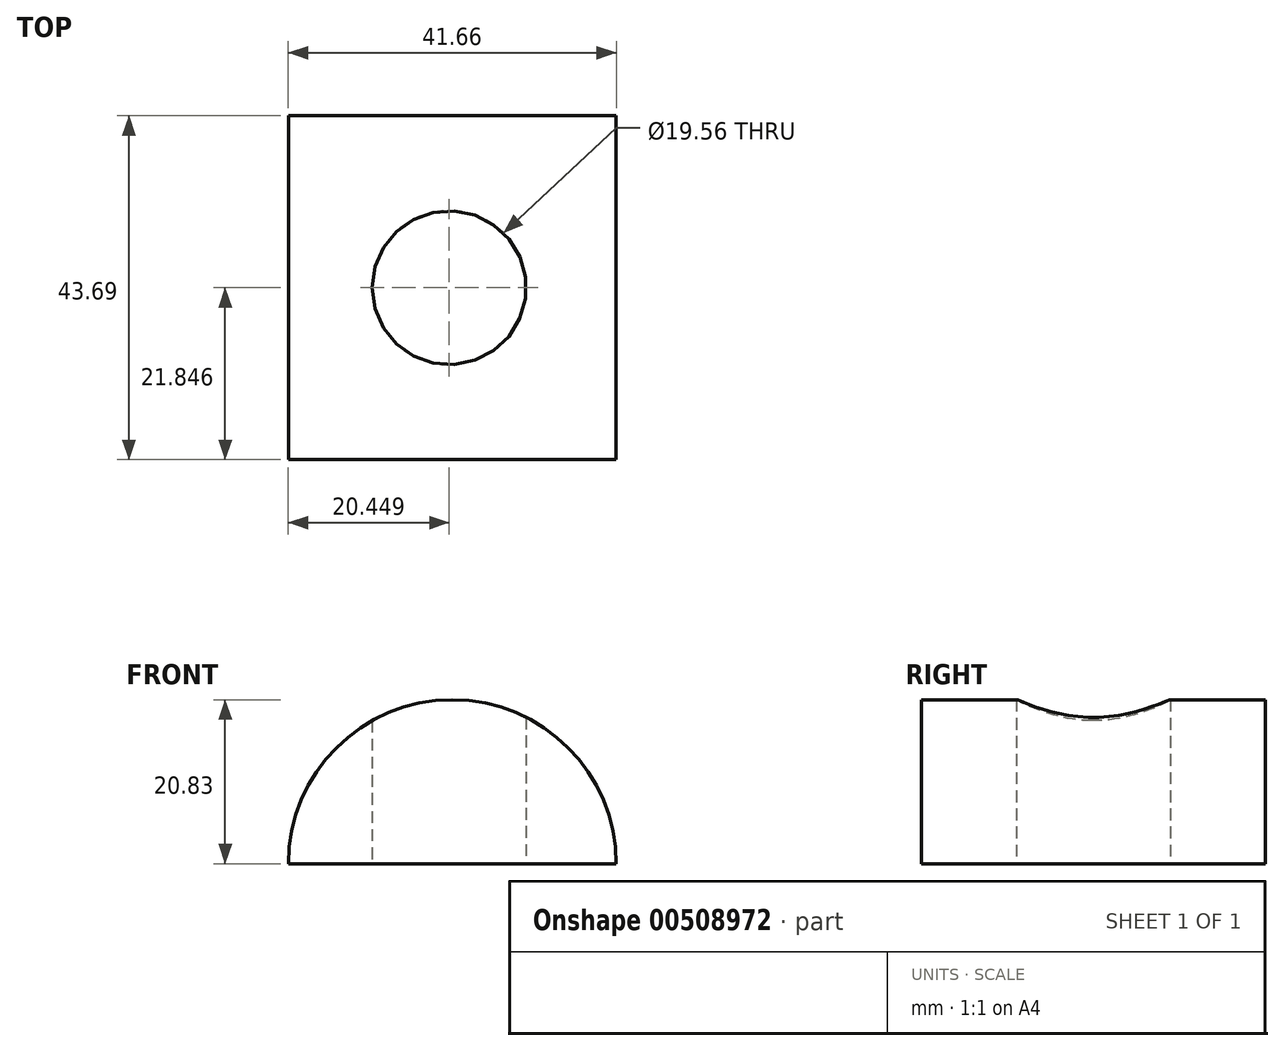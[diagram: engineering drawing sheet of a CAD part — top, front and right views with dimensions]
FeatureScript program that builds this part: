
annotation { "Feature Type Name" : "Feature", "Feature Type Description" : "" }
export const myFeature = defineFeature(function(context is Context, id is Id, definition is map)
    precondition{}
    {
        {
            var Q0;
            Q0=qCreatedBy(makeId("Top.planeOp"),FACE);
            var sketch = newSketch(context, id + "F0", { "sketchPlane" : qUnion([Q0])});
            skLineSegment(sketch, "E0.bottom", {"start": v(0, 0) * mm, "end": v(43.18, 0) * mm});
            skLineSegment(sketch, "E0.top", {"start": v(0, -43.69) * mm, "end": v(43.18, -43.69) * mm});
            skLineSegment(sketch, "E0.left", {"start": v(0, 0) * mm, "end": v(0, -43.69) * mm});
            skLineSegment(sketch, "E0.right", {"start": v(43.18, 0) * mm, "end": v(43.18, -43.69) * mm});
            skLineSegment(sketch, "E1", {"start": v(0, -21.84) * mm, "end": v(21.2, -21.84) * mm, "construction": true});
            skCircle(sketch, "E2", {"center": v(21.2, -21.84) * mm, "radius": 9.78 * mm});
            skSolve(sketch);
        }
        {
            var Q0;
            Q0=qSketchRegion(id+"F0",true);
            extrude(context, id + "F1", {"entities" : qUnion([Q0]), "depth" : 20.83 * mm});
        }
        {
            var Q0;
            Q0=makeQuery(id+"F1.opExtrude","SWEPT_FACE",FACE,{"disambiguationData":[OSD([sQuery(id+"F0.wireOp",EDGE,"E0.top")])]});
            var sketch = newSketch(context, id + "F2", { "sketchPlane" : qUnion([Q0])});
            skArc(sketch, "E3", {"start": v(42.42, 0) * mm, "mid": v(21.59, 20.83) * mm, "end": v(0.76, 0) * mm});
            skSolve(sketch);
        }
        {
            var Q0;
            {var subQ3=sQuery(id+"F2.wireOp",EDGE,"E3");Q0=makeQuery(id+"F2.imprint","IMPRINT",FACE,{"disambiguationData":[TD([[makeQuery(id+"F2.imprint","IMPRINT",EDGE,{"derivedFrom":subQ3}),-1.0]])]});}
            extrude(context, id + "F3", {"entities" : qUnion([Q0]), "operationType" : NewBodyOperationType.REMOVE, "endBound" : BoundingType.THROUGH_ALL, "oppositeDirection" : true, "depth" : 25.4 * mm});
        }
    });
